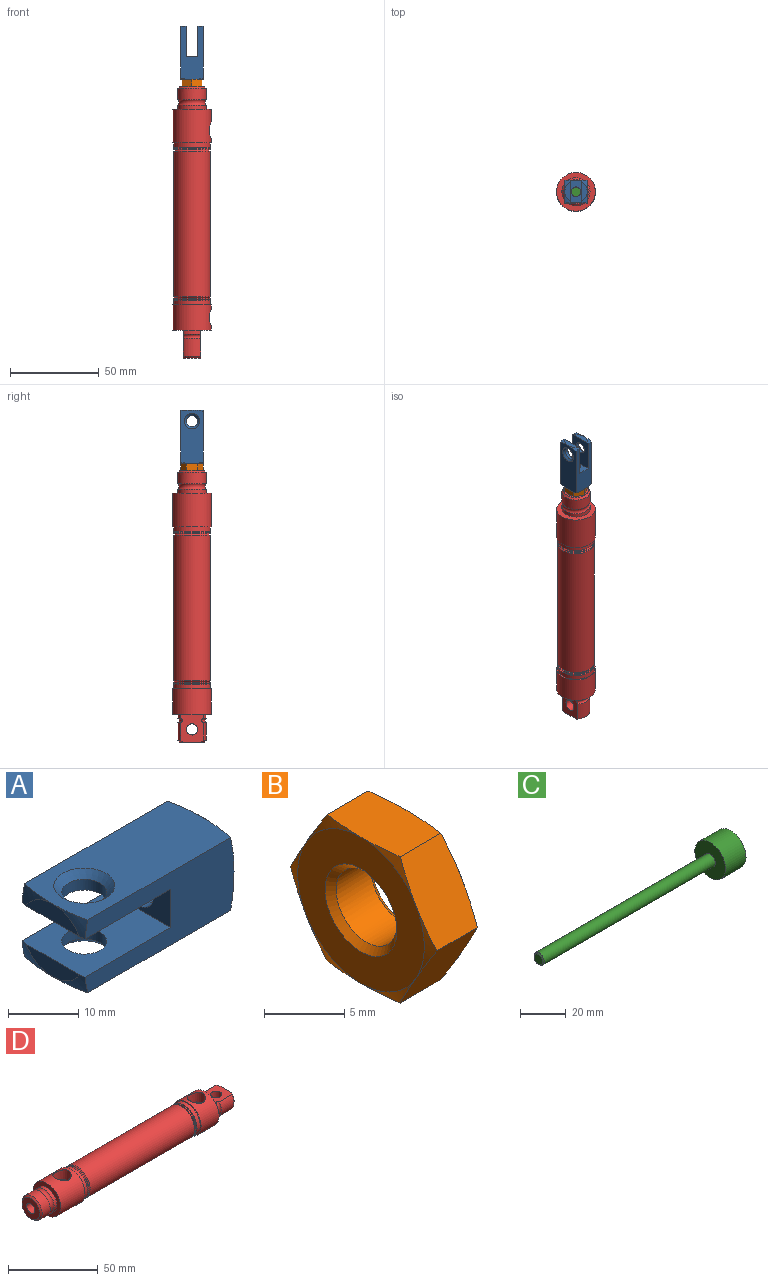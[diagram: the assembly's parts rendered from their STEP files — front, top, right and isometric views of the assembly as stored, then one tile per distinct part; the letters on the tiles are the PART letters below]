
ASSEMBLY  parts=4 mates=3
PART A: 26 faces, bbox 30.5x18.3x18.3 mm
  f0: cone r=4.34mm half-angle=45deg, axis (0,0,-1), area 38.2mm2, adj f1,f7
  f1: cylinder r=3.19mm len=6.39mm, axis (0,0,-1), area 37.6mm2, adj f0,f17
  f2: cylinder r=3.19mm len=6.39mm, axis (0,0,-1), area 37.6mm2, adj f4,f15
  f3: cylinder r=2.71mm len=5.41mm, axis (-1,0,0), area 25.9mm2, adj f16,f25
  f4: cone r=4.34mm half-angle=45deg, axis (0,0,1), area 38.2mm2, adj f2,f19
  f5: cone r=3.17mm half-angle=45deg, axis (1,0,0), area 12.8mm2, adj f6,f20
  f6: cylinder r=2.68mm len=10.68mm, axis (-1,0,0), area 180.2mm2, adj f5,f25
  f7: plane 30.18x12.7mm, normal (0,0,-1), area 318.5mm2, adj f0,f8,f9,f10,f11,f12,f13
  f8: plane 30.37x13.07mm, normal (0,-1,0), area 262.9mm2, adj f7,f9,f13,f14,f15,f16,f17,f18
  f9: torus R=3.17mm, axis (1,0,0), area 8.9mm2, adj f7,f8,f20
  f10: torus R=3.17mm, axis (1,0,0), area 8.9mm2, adj f7,f11,f20
  f11: plane 30.37x13.07mm, normal (0,1,0), area 261.5mm2, adj f7,f10,f12,f15,f16,f17,f19,f21
  f12: torus R=3.17mm, axis (1,0,0), area 8.2mm2, adj f7,f11,f17,f23
  f13: torus R=3.17mm, axis (1,0,0), area 8.2mm2, adj f7,f8,f17,f23
  f14: torus R=3.17mm, axis (1,0,0), area 8.2mm2, adj f8,f15,f19,f24
  f15: plane 17.51x12.73mm, normal (0,0,-1), area 189.7mm2, adj f2,f8,f11,f14,f16,f21,f24
  f16: plane 12.7x6.67mm, normal (-1,0,0), area 61.7mm2, adj f3,f8,f11,f15,f17
  f17: plane 17.51x12.73mm, normal (0,0,1), area 189.7mm2, adj f1,f8,f11,f12,f13,f16,f23
  f18: torus R=3.17mm, axis (1,0,0), area 8.9mm2, adj f8,f19,f20
  f19: plane 30.18x12.7mm, normal (0,0,1), area 318.5mm2, adj f4,f8,f11,f14,f18,f21,f22
  f20: plane 12.7x12.7mm, normal (1,0,0), area 95mm2, adj f5,f9,f10,f18,f22
  f21: torus R=3.17mm, axis (1,0,0), area 8.2mm2, adj f11,f15,f19,f24
  f22: torus R=3.17mm, axis (1,0,0), area 8.9mm2, adj f11,f19,f20
  f23: plane 10.81x3.02mm, normal (-1,0,0), area 23mm2, adj f12,f13,f17
  f24: plane 10.81x3.02mm, normal (-1,0,0), area 23mm2, adj f14,f15,f21
  f25: plane 5.41x5.41mm, normal (-1,0,0), area 0.4mm2, adj f3,f6
PART B: 23 faces, bbox 4.5x13.4x13.4 mm
  f0: cone r=3.17mm half-angle=45deg, axis (-1,0,0), area 12.8mm2, adj f2,f4
  f1: cone r=6.46mm half-angle=75deg, axis (1,0,0), area 2.8mm2, adj f4,f10,f11
  f2: cylinder r=2.68mm len=5.37mm, axis (-1,0,0), area 51.9mm2, adj f0,f3
  f3: cone r=3.17mm half-angle=45deg, axis (1,0,0), area 12.8mm2, adj f2,f22
  f4: plane 11.18x11.18mm, normal (-1,0,0), area 66.4mm2, adj f0,f1,f5,f6,f7,f8,f9
  f5: cone r=6.46mm half-angle=75deg, axis (1,0,0), area 2.8mm2, adj f4,f10,f12
  f6: cone r=6.46mm half-angle=75deg, axis (1,0,0), area 2.8mm2, adj f4,f12,f13
  f7: cone r=6.46mm half-angle=75deg, axis (1,0,0), area 2.8mm2, adj f4,f13,f14
  f8: cone r=6.46mm half-angle=75deg, axis (1,0,0), area 2.8mm2, adj f4,f14,f15
  f9: cone r=6.46mm half-angle=75deg, axis (1,0,0), area 2.8mm2, adj f4,f11,f15
  f10: plane 6.06x4.53mm, normal (0,0.87,-0.5), area 25.2mm2, adj f1,f5,f11,f12,f16,f17
  f11: plane 6.06x4.53mm, normal (0,0.87,0.5), area 25.2mm2, adj f1,f9,f10,f15,f17,f18
  f12: plane 6.92x4.53mm, normal (0,0,-1), area 25.2mm2, adj f5,f6,f10,f13,f16,f19
  f13: plane 6.06x4.53mm, normal (0,-0.87,-0.5), area 25.2mm2, adj f6,f7,f12,f14,f19,f20
  f14: plane 6.06x4.53mm, normal (0,-0.87,0.5), area 25.2mm2, adj f7,f8,f13,f15,f20,f21
  f15: plane 6.92x4.53mm, normal (0,0,1), area 25.2mm2, adj f8,f9,f11,f14,f18,f21
  f16: cone r=6.46mm half-angle=75deg, axis (-1,0,0), area 2.8mm2, adj f10,f12,f22
  f17: cone r=6.46mm half-angle=75deg, axis (-1,0,0), area 2.8mm2, adj f10,f11,f22
  f18: cone r=6.46mm half-angle=75deg, axis (-1,0,0), area 2.8mm2, adj f11,f15,f22
  f19: cone r=6.46mm half-angle=75deg, axis (-1,0,0), area 2.8mm2, adj f12,f13,f22
  f20: cone r=6.46mm half-angle=75deg, axis (-1,0,0), area 2.8mm2, adj f13,f14,f22
  f21: cone r=6.46mm half-angle=75deg, axis (-1,0,0), area 2.8mm2, adj f14,f15,f22
  f22: plane 11.18x11.18mm, normal (1,0,0), area 66.4mm2, adj f3,f16,f17,f18,f19,f20,f21
PART C: 6 faces, bbox 119.5x19.1x19.1 mm
  f0: cone r=2.67mm half-angle=45deg, axis (1,0,0), area 13.2mm2, adj f2,f3
  f1: cylinder r=9.53mm len=19.05mm, axis (1,0,0), area 760.1mm2, adj f4,f5
  f2: cylinder r=3.17mm len=106.3mm, axis (1,0,0), area 2120.6mm2, adj f0,f4
  f3: plane 5.33x5.33mm, normal (-1,0,0), area 22.3mm2, adj f0
  f4: plane 19.05x19.05mm, normal (-1,0,0), area 253.4mm2, adj f1,f2
  f5: plane 19.05x19.05mm, normal (1,0,0), area 285mm2, adj f1
PART D: 50 faces, bbox 153.4x22.1x22.1 mm
  f0: torus R=8.49mm, axis (-1,0,0), area 29.4mm2, adj f1,f47,f48,f49
  f1: plane 15.97x12.83mm, normal (0,0,-1), area 162.4mm2, adj f0,f2,f3,f4,f5,f43,f44,f45
  f2: cylinder r=3.17mm len=9.65mm, axis (0,0,1), area 192.5mm2, adj f1,f48
  f3: torus R=8.49mm, axis (-1,0,0), area 29.4mm2, adj f1,f4,f46,f48
  f4: cylinder r=7.94mm len=9.65mm, axis (-1,0,0), area 25mm2, adj f1,f3,f5,f48
  f5: plane 21.84x21.84mm, normal (1,0,0), area 231.6mm2, adj f1,f4,f6,f48,f49
  f6: cylinder r=10.92mm len=21.84mm, axis (-1,0,0), area 891mm2, adj f5,f7,f11
  f7: cone r=5.14mm half-angle=1.7deg, axis (0,0,1), area 219.4mm2, adj f6,f8
  f8: plane 9.87x9.87mm, normal (0,0,1), area 20.7mm2, adj f7,f9
  f9: cylinder r=4.22mm len=8.43mm, axis (0,0,1), area 124.5mm2, adj f8,f10
  f10: cone r=4.22mm half-angle=59deg, axis (0,0,1), area 65.2mm2, adj f9
  f11: plane 21.84x21.84mm, normal (-1,0,0), area 42.3mm2, adj f6,f12
  f12: cylinder r=10.29mm len=20.57mm, axis (-1,0,0), area 164.2mm2, adj f11,f13
  f13: plane 20.57x20.57mm, normal (-1,0,0), area 47.4mm2, adj f12,f14
  f14: cone r=10.29mm half-angle=45deg, axis (-1,0,0), area 67.1mm2, adj f13,f15
  f15: cylinder r=10.29mm len=20.57mm, axis (-1,0,0), area 32.8mm2, adj f14,f16
  f16: plane 20.57x20.57mm, normal (-1,0,0), area 47.4mm2, adj f15,f17
  f17: cone r=10.29mm half-angle=45deg, axis (-1,0,0), area 67.1mm2, adj f16,f18
  f18: cylinder r=10.29mm len=82.17mm, axis (-1,0,0), area 5311mm2, adj f17,f19
  f19: cone r=9.4mm half-angle=45deg, axis (1,0,0), area 77.8mm2, adj f18,f20
  f20: plane 20.57x20.57mm, normal (1,0,0), area 55mm2, adj f19,f21
  f21: cylinder r=10.29mm len=20.57mm, axis (-1,0,0), area 24.6mm2, adj f20,f22
  f22: cone r=9.4mm half-angle=45deg, axis (1,0,0), area 77.8mm2, adj f21,f23
  f23: plane 20.57x20.57mm, normal (1,0,0), area 55mm2, adj f22,f24
  f24: cylinder r=10.29mm len=20.57mm, axis (-1,0,0), area 164.2mm2, adj f23,f25
  f25: plane 21.84x21.84mm, normal (1,0,0), area 42.3mm2, adj f24,f26
  f26: cylinder r=10.92mm len=21.84mm, axis (-1,0,0), area 1222.2mm2, adj f25,f27,f42
  f27: cone r=5.14mm half-angle=1.7deg, axis (0,0,1), area 219.4mm2, adj f26,f28
  f28: plane 9.87x9.87mm, normal (0,0,1), area 20.7mm2, adj f27,f29
  f29: cylinder r=4.22mm len=8.43mm, axis (0,0,1), area 79.9mm2, adj f28,f30,f31,f32
  f30: cone r=4.22mm half-angle=59deg, axis (0,0,1), area 0mm2, adj f29,f32
  f31: cone r=4.22mm half-angle=59deg, axis (0,0,1), area 0mm2, adj f29,f32
  f32: cylinder r=3.17mm len=43.31mm, axis (1,0,0), area 778.9mm2, adj f29,f30,f31,f33,f38,f39
  f33: plane 13.84x13.84mm, normal (-1,0,0), area 118.8mm2, adj f32,f34
  f34: cone r=6.92mm half-angle=45deg, axis (1,0,0), area 67.1mm2, adj f33,f35
  f35: cylinder r=7.94mm len=15.88mm, axis (-1,0,0), area 316.7mm2, adj f34,f36
  f36: torus R=9.28mm, axis (-1,0,0), area 162.1mm2, adj f35,f37
  f37: cylinder r=7.94mm len=15.88mm, axis (-1,0,0), area 114mm2, adj f36,f42
  f38: cone r=4.22mm half-angle=59deg, axis (0,0,1), area 0mm2, adj f32
  f39: plane 19.05x19.05mm, normal (1,0,0), area 253.4mm2, adj f32,f40
  f40: cylinder r=9.53mm len=63.5mm, axis (1,0,0), area 3800.3mm2, adj f39,f41
  f41: plane 19.05x19.05mm, normal (-1,0,0), area 285mm2, adj f40
  f42: plane 21.84x21.84mm, normal (-1,0,0), area 176.8mm2, adj f26,f37
  f43: cone r=7.94mm half-angle=45deg, axis (-1,0,0), area 15.2mm2, adj f1,f44,f47,f48
  f44: plane 13.84x9.65mm, normal (1,0,0), area 121.8mm2, adj f1,f43,f45,f48
  f45: cone r=7.94mm half-angle=45deg, axis (-1,0,0), area 15.2mm2, adj f1,f44,f46,f48
  f46: cylinder r=7.94mm len=10.03mm, axis (-1,0,0), area 104.1mm2, adj f1,f3,f45,f48
  f47: cylinder r=7.94mm len=10.03mm, axis (-1,0,0), area 104.1mm2, adj f0,f1,f43,f48
  f48: plane 15.97x12.83mm, normal (0,0,1), area 162.4mm2, adj f0,f2,f3,f4,f5,f43,f44,f45
  f49: cylinder r=7.94mm len=9.65mm, axis (-1,0,0), area 25mm2, adj f0,f1,f5,f48
PLACE A rot(axis=(0,1,0),90deg) t=(0,0,27.89)mm
PLACE B rot(axis=(0.71,0,-0.71),180deg) t=(0,0,27.89)mm
PLACE C rot(axis=(0.58,0.58,-0.58),120deg) t=(0,0,336.58)mm
PLACE D rot(axis=(0,1,0),90deg) t=(0,0,0)mm fixed
MATE fastened A.f12 <-> B.f0  axis (0,0,-1) through (0,0,4.06)mm
MATE fastened B.f0 <-> C.f0  axis (0,0,-1) through (0,0,0)mm
MATE slider C.f0 <-> D.f0  axis (0,0,1) through (0,0,12.7)mm
